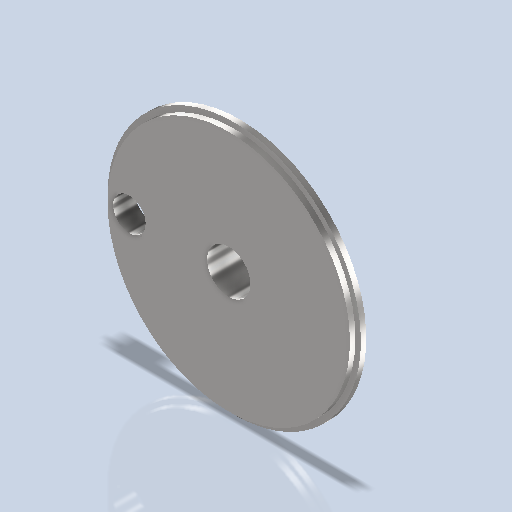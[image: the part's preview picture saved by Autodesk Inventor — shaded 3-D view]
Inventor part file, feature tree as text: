
AUTODESK INVENTOR PART (.ipt)
format: ipt  version: 2024.2 (Build 282272000, 272)  size: 279,552 bytes
history: native  units: mm
features: extrude x6, sketch x5, projected_geometry x2, fillet x1
ambient origin geometry x8: Origin, YZ Plane, XZ Plane, XY Plane, X Axis, Y Axis, Z Axis, Center Point
bodies: Volumenkörper1 (feature_tree)
feature tree (14):
  sketch  "Skizze1"  dims[d0=222.5mm d1=232.5mm]
  extrude  "Extrusion1"  Depth=232.5mm
  extrude  "Extrusion2"  Depth=5.0mm TaperAngle=0.0deg
  sketch  "Skizze2"  dims[d2=5.0mm d3=0.0mm d4=5.0mm d5=0.0mm]
  extrude  "Extrusion3"  Depth=40.0mm
  extrude  "Extrusion5"  Depth=40.0mm
  extrude  "Extrusion6"  Depth=20.0mm TaperAngle=0.0deg
  extrude  "Extrusion7"  Depth=20.0mm TaperAngle=0.0deg
  fillet  "Rundung1"  Radius=20.0mm
  sketch  "Skizze3"  dims[d6=50.0mm d7=40.0mm]
  sketch  "Skizze4"  dims[d10=20.0mm d11=0.0mm d14=40.0mm]
  projected_geometry  "Projizierte Kontur1"
  projected_geometry  "Projizierte Kontur2"
  sketch  "Skizze5"  dims[d15=30.0mm d16=20.0mm d17=0.0mm d18=20.0mm d19=0.0mm d20=20.0mm d21=0.0mm d22=5.0mm]
